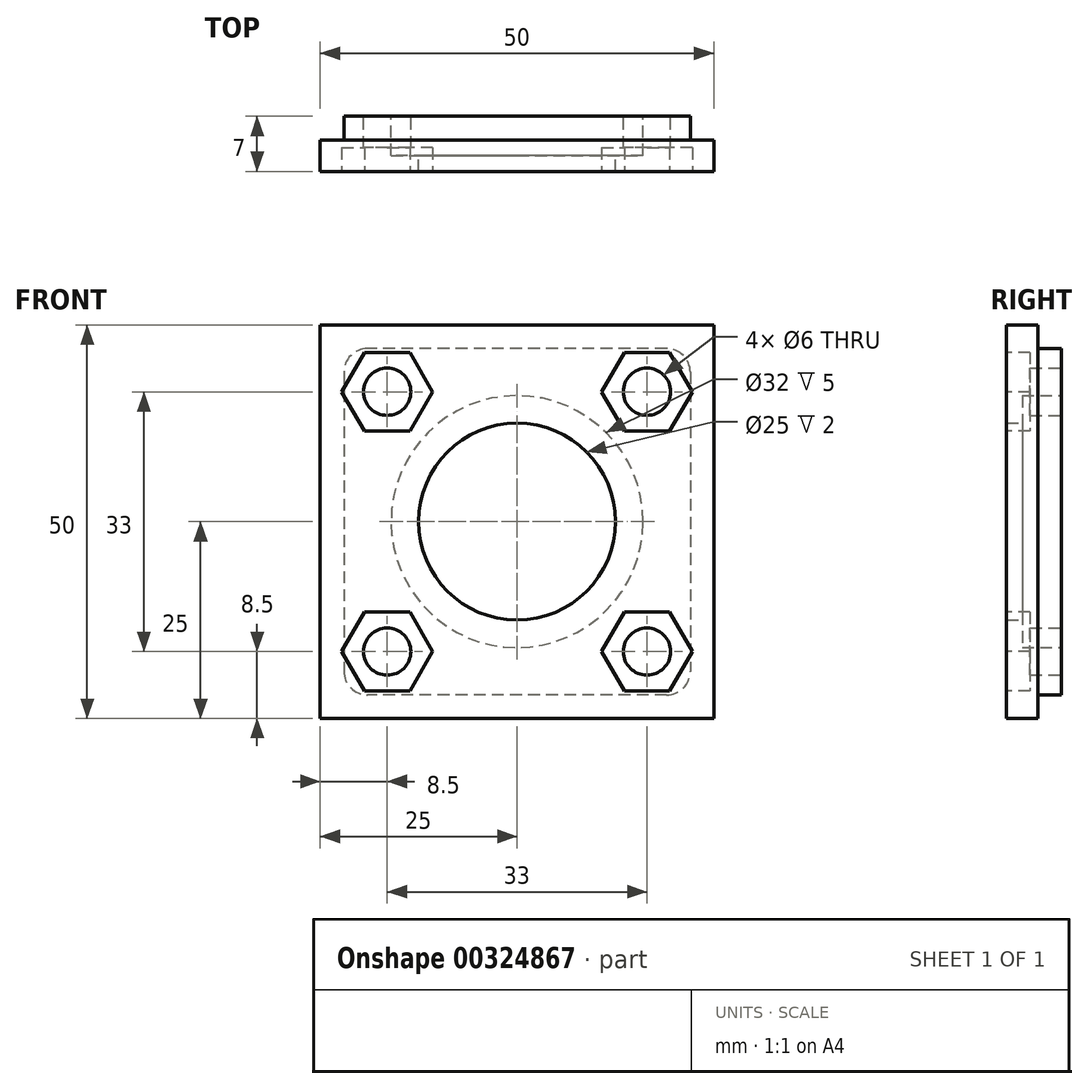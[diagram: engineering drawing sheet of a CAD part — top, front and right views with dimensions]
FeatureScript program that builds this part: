
annotation { "Feature Type Name" : "Feature", "Feature Type Description" : "" }
export const myFeature = defineFeature(function(context is Context, id is Id, definition is map)
    precondition{}
    {
        {
            var Q0;
            Q0=qCreatedBy(makeId("Front.planeOp"),FACE);
            var sketch = newSketch(context, id + "F0", { "sketchPlane" : qUnion([Q0])});
            skLineSegment(sketch, "E0.bottom", {"start": v(-25, 25) * mm, "end": v(25, 25) * mm});
            skLineSegment(sketch, "E0.top", {"start": v(-25, -25) * mm, "end": v(25, -25) * mm});
            skLineSegment(sketch, "E0.left", {"start": v(-25, 25) * mm, "end": v(-25, -25) * mm});
            skLineSegment(sketch, "E0.right", {"start": v(25, 25) * mm, "end": v(25, -25) * mm});
            skPoint(sketch, "E0.middle", {"position": v(0, 0) * mm});
            skSolve(sketch);
        }
        {
            var Q0;
            Q0=makeQuery(id+"F0.imprint","IMPRINT",FACE,{"disambiguationData":[TD([[makeQuery(id+"F0.imprint","IMPRINT",EDGE,{"derivedFrom":sQuery(id+"F0.wireOp",EDGE,"E0.bottom")}),-1.0]])]});
            extrude(context, id + "F1", {"entities" : qUnion([Q0]), "oppositeDirection" : true, "depth" : 4 * mm});
        }
        {
            var Q0;
            Q0=makeQuery(id+"F1.opExtrude","CAP_FACE",FACE,{"disambiguationData":[OSD([sQuery(id+"F0.wireOp",EDGE,"E0.bottom"),sQuery(id+"F0.wireOp",EDGE,"E0.top"),sQuery(id+"F0.wireOp",EDGE,"E0.left"),sQuery(id+"F0.wireOp",EDGE,"E0.right")])],"isStart":false});
            var sketch = newSketch(context, id + "F2", { "sketchPlane" : qUnion([Q0])});
            skLineSegment(sketch, "E1.bottom", {"start": v(-22, 22) * mm, "end": v(22, 22) * mm});
            skLineSegment(sketch, "E1.top", {"start": v(-22, -22) * mm, "end": v(22, -22) * mm});
            skLineSegment(sketch, "E1.left", {"start": v(-22, 22) * mm, "end": v(-22, -22) * mm});
            skLineSegment(sketch, "E1.right", {"start": v(22, 22) * mm, "end": v(22, -22) * mm});
            skPoint(sketch, "E1.middle", {"position": v(0, 0) * mm});
            skSolve(sketch);
        }
        {
            var Q0;
            Q0=makeQuery(id+"F2.imprint","IMPRINT",FACE,{"disambiguationData":[TD([[makeQuery(id+"F2.imprint","IMPRINT",EDGE,{"derivedFrom":sQuery(id+"F2.wireOp",EDGE,"E1.bottom")}),-1.0]])]});
            extrude(context, id + "F3", {"entities" : qUnion([Q0]), "operationType" : NewBodyOperationType.ADD, "depth" : 3 * mm});
        }
        {
            var Q0;
            Q0=makeQuery(id+"F3.opExtrude","CAP_FACE",FACE,{"disambiguationData":[OSD([sQuery(id+"F2.wireOp",EDGE,"E1.bottom"),sQuery(id+"F2.wireOp",EDGE,"E1.top"),sQuery(id+"F2.wireOp",EDGE,"E1.left"),sQuery(id+"F2.wireOp",EDGE,"E1.right")])],"isStart":false});
            var sketch = newSketch(context, id + "F4", { "sketchPlane" : qUnion([Q0])});
            skLineSegment(sketch, "E2", {"start": v(-22, 22) * mm, "end": v(22, -22) * mm, "construction": true});
            skLineSegment(sketch, "E3", {"start": v(22, 22) * mm, "end": v(-22, -22) * mm, "construction": true});
            skLineSegment(sketch, "E4.bottom", {"start": v(-16.5, 16.5) * mm, "end": v(16.5, 16.5) * mm, "construction": true});
            skLineSegment(sketch, "E4.top", {"start": v(-16.5, -16.5) * mm, "end": v(16.5, -16.5) * mm, "construction": true});
            skLineSegment(sketch, "E4.left", {"start": v(-16.5, 16.5) * mm, "end": v(-16.5, -16.5) * mm, "construction": true});
            skLineSegment(sketch, "E4.right", {"start": v(16.5, 16.5) * mm, "end": v(16.5, -16.5) * mm, "construction": true});
            skPoint(sketch, "E4.middle", {"position": v(0, 0) * mm});
            skCircle(sketch, "E5", {"center": v(-16.5, 16.5) * mm, "radius": 3 * mm});
            skCircle(sketch, "E6", {"center": v(16.5, 16.5) * mm, "radius": 3 * mm});
            skCircle(sketch, "E7", {"center": v(-16.5, -16.5) * mm, "radius": 3 * mm});
            skCircle(sketch, "E8", {"center": v(16.5, -16.5) * mm, "radius": 3 * mm});
            skCircle(sketch, "E9", {"center": v(0, 0) * mm, "radius": 7.5 * mm});
            skSolve(sketch);
        }
        {
            var Q0;
            Q0=makeQuery(id+"F4.imprint","IMPRINT",FACE,{"disambiguationData":[TD([[makeQuery(id+"F4.imprint","IMPRINT",EDGE,{"derivedFrom":sQuery(id+"F4.wireOp",EDGE,"E5")}),1.0]])]});
            var Q1;
            Q1=makeQuery(id+"F4.imprint","IMPRINT",FACE,{"disambiguationData":[TD([[makeQuery(id+"F4.imprint","IMPRINT",EDGE,{"derivedFrom":sQuery(id+"F4.wireOp",EDGE,"E6")}),1.0]])]});
            var Q2;
            Q2=makeQuery(id+"F4.imprint","IMPRINT",FACE,{"disambiguationData":[TD([[makeQuery(id+"F4.imprint","IMPRINT",EDGE,{"derivedFrom":sQuery(id+"F4.wireOp",EDGE,"E8")}),1.0]])]});
            var Q3;
            Q3=makeQuery(id+"F4.imprint","IMPRINT",FACE,{"disambiguationData":[TD([[makeQuery(id+"F4.imprint","IMPRINT",EDGE,{"derivedFrom":sQuery(id+"F4.wireOp",EDGE,"E7")}),1.0]])]});
            var Q4;
            Q4=makeQuery(id+"F4.imprint","IMPRINT",FACE,{"disambiguationData":[TD([[makeQuery(id+"F4.imprint","IMPRINT",EDGE,{"derivedFrom":sQuery(id+"F4.wireOp",EDGE,"E9")}),1.0]])]});
            extrude(context, id + "F5", {"entities" : qUnion([Q0, Q1, Q2, Q3, Q4]), "operationType" : NewBodyOperationType.REMOVE, "oppositeDirection" : true, "depth" : 25 * mm});
        }
        {
            var Q0;
            Q0=makeQuery(id+"F1.opExtrude","CAP_FACE",FACE,{"disambiguationData":[OSD([sQuery(id+"F0.wireOp",EDGE,"E0.bottom"),sQuery(id+"F0.wireOp",EDGE,"E0.top"),sQuery(id+"F0.wireOp",EDGE,"E0.left"),sQuery(id+"F0.wireOp",EDGE,"E0.right")])],"isStart":true});
            var sketch = newSketch(context, id + "F6", { "sketchPlane" : qUnion([Q0])});
            skCircle(sketch, "E10.cCircle", {"center": v(-16.5, 16.5) * mm, "radius": 5 * mm, "construction": true});
            skLineSegment(sketch, "E10.0", {"start": v(-13.61, 11.5) * mm, "end": v(-19.39, 11.5) * mm});
            skLineSegment(sketch, "E10.1", {"start": v(-19.39, 11.5) * mm, "end": v(-22.27, 16.5) * mm});
            skLineSegment(sketch, "E10.2", {"start": v(-22.27, 16.5) * mm, "end": v(-19.39, 21.5) * mm});
            skLineSegment(sketch, "E10.3", {"start": v(-19.39, 21.5) * mm, "end": v(-13.61, 21.5) * mm});
            skLineSegment(sketch, "E10.4", {"start": v(-13.61, 21.5) * mm, "end": v(-10.73, 16.5) * mm});
            skLineSegment(sketch, "E10.5", {"start": v(-10.73, 16.5) * mm, "end": v(-13.61, 11.5) * mm});
            skPoint(sketch, "E10.0.midPoint", {"position": v(-16.5, 11.5) * mm});
            skCircle(sketch, "E11.cCircle", {"center": v(-16.5, -16.5) * mm, "radius": 5 * mm, "construction": true});
            skLineSegment(sketch, "E11.0", {"start": v(-13.61, -21.5) * mm, "end": v(-19.39, -21.5) * mm});
            skLineSegment(sketch, "E11.1", {"start": v(-19.39, -21.5) * mm, "end": v(-22.27, -16.5) * mm});
            skLineSegment(sketch, "E11.2", {"start": v(-22.27, -16.5) * mm, "end": v(-19.39, -11.5) * mm});
            skLineSegment(sketch, "E11.3", {"start": v(-19.39, -11.5) * mm, "end": v(-13.61, -11.5) * mm});
            skLineSegment(sketch, "E11.4", {"start": v(-13.61, -11.5) * mm, "end": v(-10.73, -16.5) * mm});
            skLineSegment(sketch, "E11.5", {"start": v(-10.73, -16.5) * mm, "end": v(-13.61, -21.5) * mm});
            skPoint(sketch, "E11.0.midPoint", {"position": v(-16.5, -21.5) * mm});
            skCircle(sketch, "E12.cCircle", {"center": v(16.5, 16.5) * mm, "radius": 5 * mm, "construction": true});
            skLineSegment(sketch, "E12.0", {"start": v(13.61, 21.5) * mm, "end": v(19.39, 21.5) * mm});
            skLineSegment(sketch, "E12.1", {"start": v(19.39, 21.5) * mm, "end": v(22.27, 16.5) * mm});
            skLineSegment(sketch, "E12.2", {"start": v(22.27, 16.5) * mm, "end": v(19.39, 11.5) * mm});
            skLineSegment(sketch, "E12.3", {"start": v(19.39, 11.5) * mm, "end": v(13.61, 11.5) * mm});
            skLineSegment(sketch, "E12.4", {"start": v(13.61, 11.5) * mm, "end": v(10.73, 16.5) * mm});
            skLineSegment(sketch, "E12.5", {"start": v(10.73, 16.5) * mm, "end": v(13.61, 21.5) * mm});
            skPoint(sketch, "E12.0.midPoint", {"position": v(16.5, 21.5) * mm});
            skCircle(sketch, "E13.cCircle", {"center": v(16.5, -16.5) * mm, "radius": 5 * mm, "construction": true});
            skLineSegment(sketch, "E13.0", {"start": v(19.39, -21.5) * mm, "end": v(13.61, -21.5) * mm});
            skLineSegment(sketch, "E13.1", {"start": v(13.61, -21.5) * mm, "end": v(10.73, -16.5) * mm});
            skLineSegment(sketch, "E13.2", {"start": v(10.73, -16.5) * mm, "end": v(13.61, -11.5) * mm});
            skLineSegment(sketch, "E13.3", {"start": v(13.61, -11.5) * mm, "end": v(19.39, -11.5) * mm});
            skLineSegment(sketch, "E13.4", {"start": v(19.39, -11.5) * mm, "end": v(22.27, -16.5) * mm});
            skLineSegment(sketch, "E13.5", {"start": v(22.27, -16.5) * mm, "end": v(19.39, -21.5) * mm});
            skPoint(sketch, "E13.0.midPoint", {"position": v(16.5, -21.5) * mm});
            skSolve(sketch);
        }
        {
            var Q0;
            Q0=makeQuery(id+"F6.imprint","IMPRINT",FACE,{"disambiguationData":[TD([[makeQuery(id+"F6.imprint","IMPRINT",EDGE,{"derivedFrom":sQuery(id+"F6.wireOp",EDGE,"E10.0")}),-1.0]])]});
            var Q1;
            Q1=makeQuery(id+"F6.imprint","IMPRINT",FACE,{"disambiguationData":[TD([[makeQuery(id+"F6.imprint","IMPRINT",EDGE,{"derivedFrom":sQuery(id+"F6.wireOp",EDGE,"E12.0")}),-1.0]])]});
            var Q2;
            Q2=makeQuery(id+"F6.imprint","IMPRINT",FACE,{"disambiguationData":[TD([[makeQuery(id+"F6.imprint","IMPRINT",EDGE,{"derivedFrom":sQuery(id+"F6.wireOp",EDGE,"E13.0")}),-1.0]])]});
            var Q3;
            Q3=makeQuery(id+"F6.imprint","IMPRINT",FACE,{"disambiguationData":[TD([[makeQuery(id+"F6.imprint","IMPRINT",EDGE,{"derivedFrom":sQuery(id+"F6.wireOp",EDGE,"E11.0")}),-1.0]])]});
            extrude(context, id + "F7", {"entities" : qUnion([Q0, Q1, Q2, Q3]), "operationType" : NewBodyOperationType.REMOVE, "oppositeDirection" : true, "depth" : 3 * mm});
        }
        {
            var Q0;
            Q0=makeQuery(id+"F3.opExtrude","CAP_FACE",FACE,{"disambiguationData":[OSD([sQuery(id+"F2.wireOp",EDGE,"E1.bottom"),sQuery(id+"F2.wireOp",EDGE,"E1.top"),sQuery(id+"F2.wireOp",EDGE,"E1.left"),sQuery(id+"F2.wireOp",EDGE,"E1.right")])],"isStart":false});
            var sketch = newSketch(context, id + "F8", { "sketchPlane" : qUnion([Q0])});
            skCircle(sketch, "E14", {"center": v(0, 0) * mm, "radius": 12 * mm});
            skSolve(sketch);
        }
        {
            var Q0;
            Q0=makeQuery(id+"F8.imprint","IMPRINT",FACE,{"disambiguationData":[TD([[makeQuery(id+"F8.imprint","IMPRINT",EDGE,{"derivedFrom":sQuery(id+"F8.wireOp",EDGE,"E14")}),1.0]])]});
            extrude(context, id + "F9", {"entities" : qUnion([Q0]), "operationType" : NewBodyOperationType.REMOVE, "oppositeDirection" : true, "depth" : 5 * mm});
        }
        {
            var Q0;
            Q0=makeQuery(id+"F3.opExtrude","CAP_FACE",FACE,{"disambiguationData":[OSD([sQuery(id+"F2.wireOp",EDGE,"E1.bottom"),sQuery(id+"F2.wireOp",EDGE,"E1.top"),sQuery(id+"F2.wireOp",EDGE,"E1.left"),sQuery(id+"F2.wireOp",EDGE,"E1.right")])],"isStart":false});
            var sketch = newSketch(context, id + "F10", { "sketchPlane" : qUnion([Q0])});
            skCircle(sketch, "E15", {"center": v(0, 0) * mm, "radius": 16 * mm});
            skSolve(sketch);
        }
        {
            var Q0;
            Q0=makeQuery(id+"F10.imprint","IMPRINT",FACE,{"disambiguationData":[TD([[makeQuery(id+"F10.imprint","IMPRINT",EDGE,{"derivedFrom":sQuery(id+"F10.wireOp",EDGE,"E15")}),1.0]])]});
            extrude(context, id + "F11", {"entities" : qUnion([Q0]), "operationType" : NewBodyOperationType.REMOVE, "oppositeDirection" : true, "depth" : 5 * mm});
        }
        {
            var Q0;
            {var subQ0=sQuery(id+"F8.wireOp",EDGE,"E14");Q0=makeQuery(id+"F11.boolean.opBoolean","MERGE",FACE,{"derivedFrom":[makeQuery(id+"F9.boolean.opBoolean","COPY",FACE,{"derivedFrom":makeQuery(id+"F9.opExtrude","CAP_FACE",FACE,{"disambiguationData":[OSD([sQuery(id+"F4.wireOp",EDGE,"E9"),subQ0])],"isStart":false})}),makeQuery(id+"F11.opExtrude","CAP_FACE",FACE,{"disambiguationData":[OSD([subQ0,sQuery(id+"F10.wireOp",EDGE,"E15")])],"isStart":false})]});}
            var sketch = newSketch(context, id + "F12", { "sketchPlane" : qUnion([Q0])});
            skCircle(sketch, "E16", {"center": v(0, 0) * mm, "radius": 12.5 * mm});
            skSolve(sketch);
        }
        {
            var Q0;
            Q0=makeQuery(id+"F12.imprint","IMPRINT",FACE,{"disambiguationData":[TD([[makeQuery(id+"F12.imprint","IMPRINT",EDGE,{"derivedFrom":sQuery(id+"F12.wireOp",EDGE,"E16")}),1.0]])]});
            extrude(context, id + "F13", {"entities" : qUnion([Q0]), "operationType" : NewBodyOperationType.REMOVE, "endBound" : BoundingType.THROUGH_ALL, "oppositeDirection" : true, "depth" : 1 * mm});
        }
        {
            var Q0;
            Q0=makeQuery(id+"F3.opExtrude","SWEPT_EDGE",EDGE,{"disambiguationData":[OSD([sQuery(id+"F2.wireOp",EDGE,"E1.bottom"),sQuery(id+"F2.wireOp",EDGE,"E1.left")])]});
            var Q1;
            Q1=makeQuery(id+"F3.opExtrude","SWEPT_EDGE",EDGE,{"disambiguationData":[OSD([sQuery(id+"F2.wireOp",EDGE,"E1.bottom"),sQuery(id+"F2.wireOp",EDGE,"E1.right")])]});
            var Q2;
            Q2=makeQuery(id+"F3.opExtrude","SWEPT_EDGE",EDGE,{"disambiguationData":[OSD([sQuery(id+"F2.wireOp",EDGE,"E1.top"),sQuery(id+"F2.wireOp",EDGE,"E1.right")])]});
            var Q3;
            Q3=makeQuery(id+"F3.opExtrude","SWEPT_EDGE",EDGE,{"disambiguationData":[OSD([sQuery(id+"F2.wireOp",EDGE,"E1.top"),sQuery(id+"F2.wireOp",EDGE,"E1.left")])]});
            fillet(context, id + "F14", {"entities" : qUnion([Q0, Q1, Q2, Q3]), "radius" : 3 * mm, "tangentPropagation" : true, "allowEdgeOverflow" : false});
        }
    });
